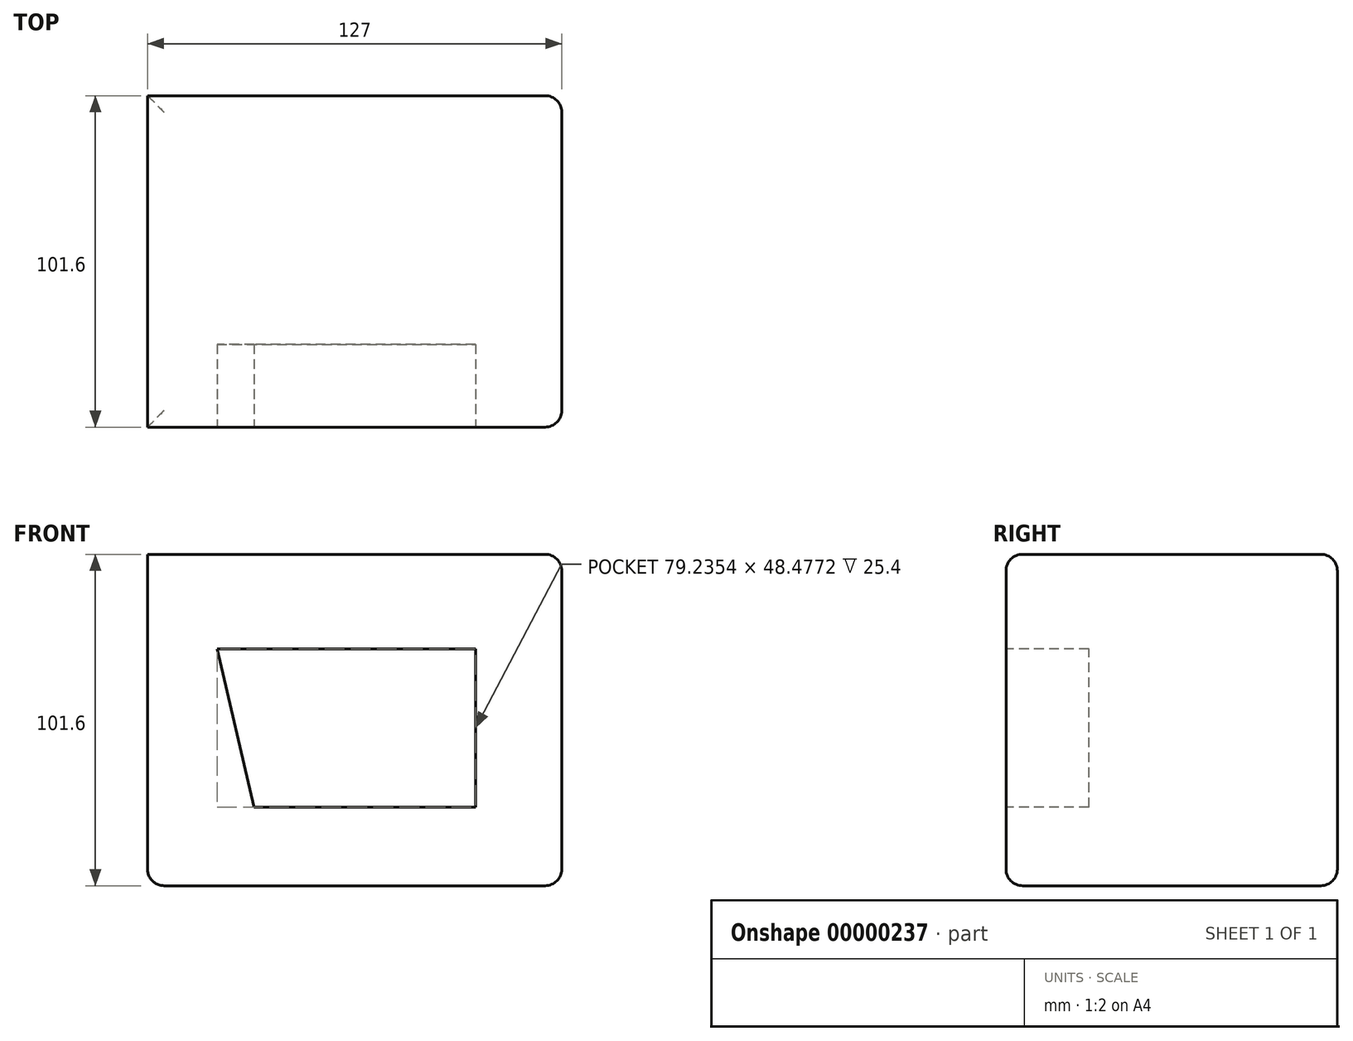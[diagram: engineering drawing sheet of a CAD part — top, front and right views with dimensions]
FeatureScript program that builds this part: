
annotation { "Feature Type Name" : "Feature", "Feature Type Description" : "" }
export const myFeature = defineFeature(function(context is Context, id is Id, definition is map)
    precondition{}
    {
        {
            var Q0;
            Q0=qCreatedBy(makeId("Right.planeOp"),FACE);
            var sketch = newSketch(context, id + "F0", { "sketchPlane" : qUnion([Q0])});
            skLineSegment(sketch, "E0", {"start": v(-50.8, 50.8) * mm, "end": v(50.8, 50.8) * mm});
            skLineSegment(sketch, "E1", {"start": v(50.8, 50.8) * mm, "end": v(50.8, -50.8) * mm});
            skLineSegment(sketch, "E2", {"start": v(50.8, -50.8) * mm, "end": v(-50.8, -50.8) * mm});
            skLineSegment(sketch, "E3", {"start": v(-50.8, -50.8) * mm, "end": v(-50.8, 50.8) * mm});
            skLineSegment(sketch, "E4", {"start": v(0, 50.8) * mm, "end": v(0, -50.8) * mm, "construction": true});
            skSolve(sketch);
        }
        {
            var Q0;
            Q0=makeQuery(id+"F0.imprint","IMPRINT",FACE,{"disambiguationData":[TD([[makeQuery(id+"F0.imprint","IMPRINT",EDGE,{"derivedFrom":sQuery(id+"F0.wireOp",EDGE,"E0")}),-1.0]])]});
            extrude(context, id + "F1", {"entities" : qUnion([Q0]), "depth" : 127 * mm, "symmetric" : true});
        }
        {
            var Q0;
            Q0=makeQuery(id+"F1.opExtrude","SWEPT_EDGE",EDGE,{"disambiguationData":[OSD([sQuery(id+"F0.wireOp",EDGE,"E0"),sQuery(id+"F0.wireOp",EDGE,"E3")])]});
            var Q1;
            Q1=makeQuery(id+"F1.opExtrude","CAP_EDGE",EDGE,{"disambiguationData":[OSD([sQuery(id+"F0.wireOp",EDGE,"E0")])],"isStart":false});
            var Q2;
            Q2=makeQuery(id+"F1.opExtrude","CAP_EDGE",EDGE,{"disambiguationData":[OSD([sQuery(id+"F0.wireOp",EDGE,"E3")])],"isStart":false});
            var Q3;
            Q3=makeQuery(id+"F1.opExtrude","CAP_EDGE",EDGE,{"disambiguationData":[OSD([sQuery(id+"F0.wireOp",EDGE,"E1")])],"isStart":false});
            var Q4;
            Q4=makeQuery(id+"F1.opExtrude","SWEPT_EDGE",EDGE,{"disambiguationData":[OSD([sQuery(id+"F0.wireOp",EDGE,"E0"),sQuery(id+"F0.wireOp",EDGE,"E1")])]});
            var Q5;
            Q5=makeQuery(id+"F1.opExtrude","CAP_EDGE",EDGE,{"disambiguationData":[OSD([sQuery(id+"F0.wireOp",EDGE,"E2")])],"isStart":false});
            var Q6;
            Q6=makeQuery(id+"F1.opExtrude","SWEPT_EDGE",EDGE,{"disambiguationData":[OSD([sQuery(id+"F0.wireOp",EDGE,"E1"),sQuery(id+"F0.wireOp",EDGE,"E2")])]});
            var Q7;
            Q7=makeQuery(id+"F1.opExtrude","SWEPT_EDGE",EDGE,{"disambiguationData":[OSD([sQuery(id+"F0.wireOp",EDGE,"E2"),sQuery(id+"F0.wireOp",EDGE,"E3")])]});
            var Q8;
            Q8=makeQuery(id+"F1.opExtrude","CAP_EDGE",EDGE,{"disambiguationData":[OSD([sQuery(id+"F0.wireOp",EDGE,"E2")])],"isStart":true});
            fillet(context, id + "F2", {"entities" : qUnion([Q0, Q1, Q2, Q3, Q4, Q5, Q6, Q7, Q8]), "radius" : 5.08 * mm, "tangentPropagation" : true, "allowEdgeOverflow" : false});
        }
        {
            var Q0;
            Q0=makeQuery(id+"F1.opExtrude","SWEPT_FACE",FACE,{"disambiguationData":[OSD([sQuery(id+"F0.wireOp",EDGE,"E3")])]});
            var sketch = newSketch(context, id + "F3", { "sketchPlane" : qUnion([Q0])});
            skLineSegment(sketch, "E5", {"start": v(-42.18, 21.74) * mm, "end": v(37.06, 21.74) * mm});
            skLineSegment(sketch, "E6", {"start": v(37.06, 21.74) * mm, "end": v(37.06, -26.74) * mm});
            skLineSegment(sketch, "E7", {"start": v(37.06, -26.74) * mm, "end": v(-30.8, -26.74) * mm});
            skLineSegment(sketch, "E8", {"start": v(-30.8, -26.74) * mm, "end": v(-42.18, 21.74) * mm});
            skSolve(sketch);
        }
        {
            var Q0;
            Q0=makeQuery(id+"F3.imprint","IMPRINT",FACE,{"disambiguationData":[TD([[makeQuery(id+"F3.imprint","IMPRINT",EDGE,{"derivedFrom":sQuery(id+"F3.wireOp",EDGE,"E5")}),-1.0]])]});
            extrude(context, id + "F4", {"entities" : qUnion([Q0]), "operationType" : NewBodyOperationType.REMOVE, "oppositeDirection" : true, "depth" : 25.4 * mm});
        }
    });
